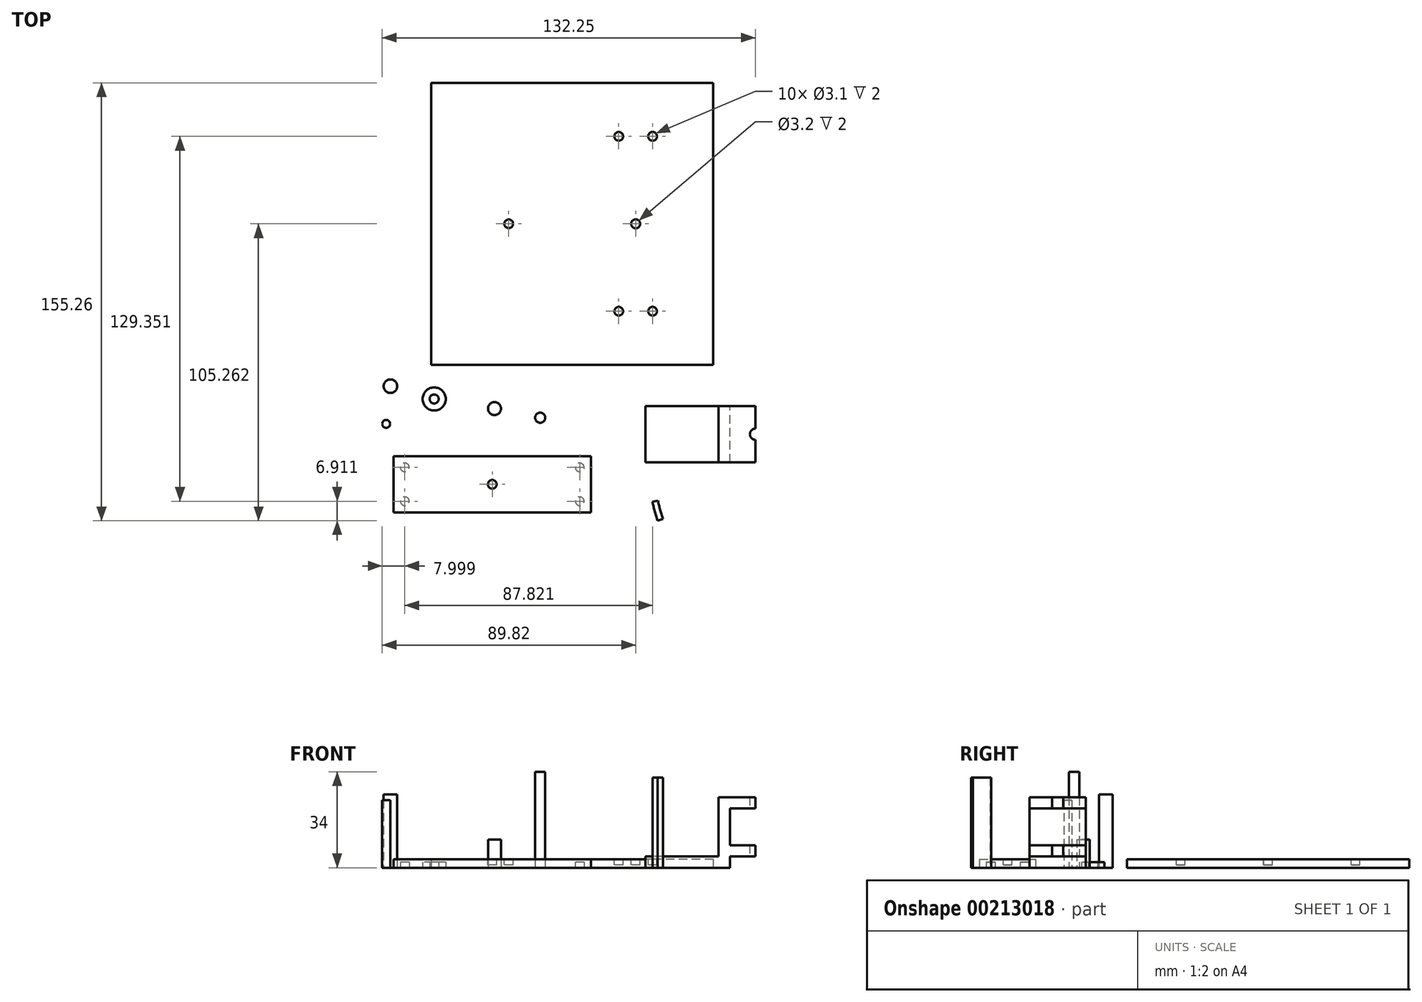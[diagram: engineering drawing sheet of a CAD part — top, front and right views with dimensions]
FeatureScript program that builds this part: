
annotation { "Feature Type Name" : "Feature", "Feature Type Description" : "" }
export const myFeature = defineFeature(function(context is Context, id is Id, definition is map)
    precondition{}
    {
        {
            var Q0;
            Q0=qCreatedBy(makeId("Top.planeOp"),FACE);
            var sketch = newSketch(context, id + "F0", { "sketchPlane" : qUnion([Q0])});
            skCircle(sketch, "E0", {"center": v(-48.92, 16) * mm, "radius": 1.6 * mm});
            skCircle(sketch, "E1", {"center": v(-48.92, 16) * mm, "radius": 4.1 * mm});
            skText(sketch, "E2", { "text": "Washer A", "fontName": "OpenSans-Regular.ttf"});
            skLineSegment(sketch, "E3.bottom", {"start": v(50, 128.1) * mm, "end": v(-50, 128.1) * mm});
            skLineSegment(sketch, "E3.top", {"start": v(50, 28.1) * mm, "end": v(-50, 28.1) * mm});
            skLineSegment(sketch, "E3.left", {"start": v(50, 128.1) * mm, "end": v(50, 28.1) * mm});
            skLineSegment(sketch, "E3.right", {"start": v(-50, 128.1) * mm, "end": v(-50, 28.1) * mm});
            skPoint(sketch, "E3.middle", {"position": v(0, 78.1) * mm});
            skLineSegment(sketch, "E4", {"start": v(-50, 78.1) * mm, "end": v(50, 78.1) * mm, "construction": true});
            skCircle(sketch, "E5", {"center": v(-64.43, 20.53) * mm, "radius": 2.4 * mm});
            skCircle(sketch, "E6", {"center": v(-28.32, -14.26) * mm, "radius": 1.6 * mm, "construction": true});
            skLineSegment(sketch, "E7.bottom", {"start": v(6.68, -24.26) * mm, "end": v(6.68, -4.26) * mm});
            skLineSegment(sketch, "E7.top", {"start": v(-63.32, -24.26) * mm, "end": v(-63.32, -4.26) * mm});
            skLineSegment(sketch, "E7.left", {"start": v(6.68, -24.26) * mm, "end": v(-63.32, -24.26) * mm});
            skLineSegment(sketch, "E7.right", {"start": v(6.68, -4.26) * mm, "end": v(-63.32, -4.26) * mm});
            skCircle(sketch, "E8", {"center": v(-59.32, -8.26) * mm, "radius": 1.55 * mm});
            skCircle(sketch, "E9", {"center": v(-59.32, -20.26) * mm, "radius": 1.55 * mm});
            skCircle(sketch, "E10", {"center": v(2.68, -8.26) * mm, "radius": 1.55 * mm});
            skCircle(sketch, "E11", {"center": v(2.68, -20.26) * mm, "radius": 1.55 * mm});
            skCircle(sketch, "E12", {"center": v(-27.53, 12.59) * mm, "radius": 2.3 * mm});
            skCircle(sketch, "E13", {"center": v(-65.92, 7.17) * mm, "radius": 1.4 * mm});
            skCircle(sketch, "E14", {"center": v(-11.34, 9.35) * mm, "radius": 1.8 * mm});
            skLineSegment(sketch, "E15.bottom", {"start": v(55.93, -6.5) * mm, "end": v(25.93, -6.5) * mm});
            skLineSegment(sketch, "E15.top", {"start": v(55.93, 13.5) * mm, "end": v(25.93, 13.5) * mm});
            skLineSegment(sketch, "E15.left", {"start": v(55.93, -6.5) * mm, "end": v(55.93, 13.5) * mm});
            skLineSegment(sketch, "E15.right", {"start": v(25.93, -6.5) * mm, "end": v(25.93, 13.5) * mm});
            skPoint(sketch, "E15.middle", {"position": v(40.93, 3.5) * mm});
            skArc(sketch, "E16", {"start": v(30.42, -20.02) * mm, "mid": v(31.18, -23.3) * mm, "end": v(32.16, -26.52) * mm});
            skLineSegment(sketch, "E17", {"start": v(32.16, -26.52) * mm, "end": v(30.27, -27.17) * mm});
            skLineSegment(sketch, "E18", {"start": v(30.42, -20.02) * mm, "end": v(28.46, -20.41) * mm});
            skArc(sketch, "E19", {"start": v(28.46, -20.41) * mm, "mid": v(29.25, -23.82) * mm, "end": v(30.27, -27.17) * mm});
            const initialGuessF0  = {"E2": [-0.05793, 0.00842, 1, 0, 0.00273]};
            skSetInitialGuess(sketch, initialGuessF0);
            skSolve(sketch);
        }
        {
            var Q0;
            Q0=makeQuery(id+"F0.imprint","IMPRINT",FACE,{"disambiguationData":[TD([[makeQuery(id+"F0.imprint","IMPRINT",EDGE,{"derivedFrom":sQuery(id+"F0.wireOp",EDGE,"E3.bottom")}),1.0]])]});
            extrude(context, id + "F1", {"entities" : qUnion([Q0]), "depth" : 3 * mm});
        }
        {
            var Q0;
            Q0=makeQuery(id+"F1.opExtrude","CAP_FACE",FACE,{"disambiguationData":[OSD([sQuery(id+"F0.wireOp",EDGE,"E3.bottom"),sQuery(id+"F0.wireOp",EDGE,"E3.top"),sQuery(id+"F0.wireOp",EDGE,"E3.left"),sQuery(id+"F0.wireOp",EDGE,"E3.right")])],"isStart":false});
            var sketch = newSketch(context, id + "F2", { "sketchPlane" : qUnion([Q0])});
            skLineSegment(sketch, "E20", {"start": v(-50, 78.1) * mm, "end": v(50, 78.1) * mm, "construction": true});
            skCircle(sketch, "E21", {"center": v(-22.5, 78.1) * mm, "radius": 1.55 * mm});
            skCircle(sketch, "E22", {"center": v(22.5, 78.1) * mm, "radius": 1.6 * mm});
            skCircle(sketch, "E23", {"center": v(-22.5, 78.1) * mm, "radius": 46 * mm, "construction": true});
            skLineSegment(sketch, "E24.bottom", {"start": v(32.5, 113.1) * mm, "end": v(12.5, 113.1) * mm, "construction": true});
            skLineSegment(sketch, "E24.top", {"start": v(32.5, 43.1) * mm, "end": v(12.5, 43.1) * mm, "construction": true});
            skLineSegment(sketch, "E24.left", {"start": v(32.5, 113.1) * mm, "end": v(32.5, 43.1) * mm, "construction": true});
            skLineSegment(sketch, "E24.right", {"start": v(12.5, 113.1) * mm, "end": v(12.5, 43.1) * mm, "construction": true});
            skCircle(sketch, "E25", {"center": v(16.5, 47.1) * mm, "radius": 1.55 * mm});
            skCircle(sketch, "E26", {"center": v(28.5, 47.1) * mm, "radius": 1.55 * mm});
            skCircle(sketch, "E27", {"center": v(16.5, 109.1) * mm, "radius": 1.55 * mm});
            skCircle(sketch, "E28", {"center": v(28.5, 109.1) * mm, "radius": 1.55 * mm});
            skSolve(sketch);
        }
        {
            var Q0;
            Q0=makeQuery(id+"F2.imprint","IMPRINT",FACE,{"disambiguationData":[TD([[makeQuery(id+"F2.imprint","IMPRINT",EDGE,{"derivedFrom":sQuery(id+"F2.wireOp",EDGE,"E21")}),1.0]])]});
            var Q1;
            Q1=makeQuery(id+"F2.imprint","IMPRINT",FACE,{"disambiguationData":[TD([[makeQuery(id+"F2.imprint","IMPRINT",EDGE,{"derivedFrom":sQuery(id+"F2.wireOp",EDGE,"E22")}),1.0]])]});
            extrude(context, id + "F3", {"entities" : qUnion([Q0, Q1]), "operationType" : NewBodyOperationType.REMOVE, "oppositeDirection" : true, "depth" : 2 * mm});
        }
        {
            var Q0;
            Q0=makeQuery(id+"F0.imprint","IMPRINT",FACE,{"disambiguationData":[TD([[makeQuery(id+"F0.imprint","IMPRINT",EDGE,{"derivedFrom":sQuery(id+"F0.wireOp",EDGE,"E5")}),1.0]])]});
            extrude(context, id + "F4", {"entities" : qUnion([Q0]), "depth" : 26 * mm});
        }
        {
            var Q0;
            Q0=makeQuery(id+"F0.imprint","IMPRINT",FACE,{"disambiguationData":[TD([[makeQuery(id+"F0.imprint","IMPRINT",EDGE,{"derivedFrom":sQuery(id+"F0.wireOp",EDGE,"E0")}),-1.0]])]});
            extrude(context, id + "F5", {"entities" : qUnion([Q0]), "depth" : 2 * mm});
        }
        {
            var Q0;
            Q0=makeQuery(id+"F0.imprint","IMPRINT",FACE,{"disambiguationData":[TD([[makeQuery(id+"F0.imprint","IMPRINT",EDGE,{"derivedFrom":sQuery(id+"F0.wireOp",EDGE,"E7.bottom")}),1.0]])]});
            var Q1;
            Q1=makeQuery(id+"F0.imprint","IMPRINT",FACE,{"disambiguationData":[TD([[makeQuery(id+"F0.imprint","IMPRINT",EDGE,{"derivedFrom":sQuery(id+"F0.wireOp",EDGE,"E8")}),1.0]])]});
            var Q2;
            Q2=makeQuery(id+"F0.imprint","IMPRINT",FACE,{"disambiguationData":[TD([[makeQuery(id+"F0.imprint","IMPRINT",EDGE,{"derivedFrom":sQuery(id+"F0.wireOp",EDGE,"E9")}),1.0]])]});
            var Q3;
            Q3=makeQuery(id+"F0.imprint","IMPRINT",FACE,{"disambiguationData":[TD([[makeQuery(id+"F0.imprint","IMPRINT",EDGE,{"derivedFrom":sQuery(id+"F0.wireOp",EDGE,"E10")}),1.0]])]});
            var Q4;
            Q4=makeQuery(id+"F0.imprint","IMPRINT",FACE,{"disambiguationData":[TD([[makeQuery(id+"F0.imprint","IMPRINT",EDGE,{"derivedFrom":sQuery(id+"F0.wireOp",EDGE,"E11")}),1.0]])]});
            extrude(context, id + "F6", {"entities" : qUnion([Q0, Q1, Q2, Q3, Q4]), "depth" : 3 * mm});
        }
        {
            var Q0;
            Q0=makeQuery(id+"F0.imprint","IMPRINT",FACE,{"disambiguationData":[TD([[makeQuery(id+"F0.imprint","IMPRINT",EDGE,{"derivedFrom":sQuery(id+"F0.wireOp",EDGE,"E10")}),1.0]])]});
            var Q1;
            Q1=makeQuery(id+"F0.imprint","IMPRINT",FACE,{"disambiguationData":[TD([[makeQuery(id+"F0.imprint","IMPRINT",EDGE,{"derivedFrom":sQuery(id+"F0.wireOp",EDGE,"E11")}),1.0]])]});
            var Q2;
            Q2=makeQuery(id+"F0.imprint","IMPRINT",FACE,{"disambiguationData":[TD([[makeQuery(id+"F0.imprint","IMPRINT",EDGE,{"derivedFrom":sQuery(id+"F0.wireOp",EDGE,"E8")}),1.0]])]});
            var Q3;
            Q3=makeQuery(id+"F0.imprint","IMPRINT",FACE,{"disambiguationData":[TD([[makeQuery(id+"F0.imprint","IMPRINT",EDGE,{"derivedFrom":sQuery(id+"F0.wireOp",EDGE,"E9")}),1.0]])]});
            extrude(context, id + "F7", {"entities" : qUnion([Q0, Q1, Q2, Q3]), "operationType" : NewBodyOperationType.REMOVE, "depth" : 2 * mm});
        }
        {
            var Q0;
            Q0=makeQuery(id+"F6.opExtrude","CAP_FACE",FACE,{"disambiguationData":[OSD([sQuery(id+"F0.wireOp",EDGE,"E7.bottom"),sQuery(id+"F0.wireOp",EDGE,"E7.top"),sQuery(id+"F0.wireOp",EDGE,"E7.left"),sQuery(id+"F0.wireOp",EDGE,"E7.right")])],"isStart":false});
            var sketch = newSketch(context, id + "F8", { "sketchPlane" : qUnion([Q0])});
            skCircle(sketch, "E29", {"center": v(-28.32, -14.26) * mm, "radius": 1.55 * mm});
            skSolve(sketch);
        }
        {
            var Q0;
            Q0=makeQuery(id+"F8.imprint","IMPRINT",FACE,{"disambiguationData":[TD([[makeQuery(id+"F8.imprint","IMPRINT",EDGE,{"derivedFrom":sQuery(id+"F8.wireOp",EDGE,"E29")}),1.0]])]});
            extrude(context, id + "F9", {"entities" : qUnion([Q0]), "operationType" : NewBodyOperationType.REMOVE, "oppositeDirection" : true, "depth" : 2 * mm});
        }
        {
            var Q0;
            Q0=makeQuery(id+"F2.imprint","IMPRINT",FACE,{"disambiguationData":[TD([[makeQuery(id+"F2.imprint","IMPRINT",EDGE,{"derivedFrom":sQuery(id+"F2.wireOp",EDGE,"E28")}),1.0]])]});
            var Q1;
            Q1=makeQuery(id+"F2.imprint","IMPRINT",FACE,{"disambiguationData":[TD([[makeQuery(id+"F2.imprint","IMPRINT",EDGE,{"derivedFrom":sQuery(id+"F2.wireOp",EDGE,"E27")}),1.0]])]});
            var Q2;
            Q2=makeQuery(id+"F2.imprint","IMPRINT",FACE,{"disambiguationData":[TD([[makeQuery(id+"F2.imprint","IMPRINT",EDGE,{"derivedFrom":sQuery(id+"F2.wireOp",EDGE,"E25")}),1.0]])]});
            var Q3;
            Q3=makeQuery(id+"F2.imprint","IMPRINT",FACE,{"disambiguationData":[TD([[makeQuery(id+"F2.imprint","IMPRINT",EDGE,{"derivedFrom":sQuery(id+"F2.wireOp",EDGE,"E26")}),1.0]])]});
            extrude(context, id + "F10", {"entities" : qUnion([Q0, Q1, Q2, Q3]), "operationType" : NewBodyOperationType.REMOVE, "oppositeDirection" : true, "depth" : 2 * mm});
        }
        {
            var Q0;
            Q0=makeQuery(id+"F0.imprint","IMPRINT",FACE,{"disambiguationData":[TD([[makeQuery(id+"F0.imprint","IMPRINT",EDGE,{"derivedFrom":sQuery(id+"F0.wireOp",EDGE,"E12")}),1.0]])]});
            extrude(context, id + "F11", {"entities" : qUnion([Q0]), "depth" : 10 * mm});
        }
        {
            var Q0;
            Q0=makeQuery(id+"F0.imprint","IMPRINT",FACE,{"disambiguationData":[TD([[makeQuery(id+"F0.imprint","IMPRINT",EDGE,{"derivedFrom":sQuery(id+"F0.wireOp",EDGE,"E13")}),1.0]])]});
            extrude(context, id + "F12", {"entities" : qUnion([Q0]), "depth" : 24 * mm});
        }
        {
            var Q0;
            Q0=makeQuery(id+"F0.imprint","IMPRINT",FACE,{"disambiguationData":[TD([[makeQuery(id+"F0.imprint","IMPRINT",EDGE,{"derivedFrom":sQuery(id+"F0.wireOp",EDGE,"E14")}),1.0]])]});
            extrude(context, id + "F13", {"entities" : qUnion([Q0]), "depth" : 34 * mm});
        }
        {
            var Q0;
            Q0=makeQuery(id+"F0.imprint","IMPRINT",FACE,{"disambiguationData":[TD([[makeQuery(id+"F0.imprint","IMPRINT",EDGE,{"derivedFrom":sQuery(id+"F0.wireOp",EDGE,"E15.bottom")}),-1.0]])]});
            extrude(context, id + "F14", {"entities" : qUnion([Q0]), "depth" : 4 * mm});
        }
        {
            var Q0;
            Q0=makeQuery(id+"F14.opExtrude","CAP_FACE",FACE,{"disambiguationData":[OSD([sQuery(id+"F0.wireOp",EDGE,"E15.bottom"),sQuery(id+"F0.wireOp",EDGE,"E15.top"),sQuery(id+"F0.wireOp",EDGE,"E15.left"),sQuery(id+"F0.wireOp",EDGE,"E15.right")])],"isStart":false});
            var sketch = newSketch(context, id + "F15", { "sketchPlane" : qUnion([Q0])});
            skLineSegment(sketch, "E30.bottom", {"start": v(55.93, 13.5) * mm, "end": v(51.93, 13.5) * mm});
            skLineSegment(sketch, "E30.top", {"start": v(55.93, -6.5) * mm, "end": v(51.93, -6.5) * mm});
            skLineSegment(sketch, "E30.left", {"start": v(55.93, 13.5) * mm, "end": v(55.93, -6.5) * mm});
            skLineSegment(sketch, "E30.right", {"start": v(51.93, 13.5) * mm, "end": v(51.93, -6.5) * mm});
            skLineSegment(sketch, "E31.bottom", {"start": v(55.93, 13.5) * mm, "end": v(64.93, 13.5) * mm});
            skLineSegment(sketch, "E31.top", {"start": v(55.93, -6.5) * mm, "end": v(64.93, -6.5) * mm});
            skLineSegment(sketch, "E31.right", {"start": v(64.93, 13.5) * mm, "end": v(64.93, -6.5) * mm});
            skCircle(sketch, "E32", {"center": v(64.93, 3.5) * mm, "radius": 1.95 * mm});
            skSolve(sketch);
        }
        {
            var Q0;
            Q0=makeQuery(id+"F15.imprint","IMPRINT",FACE,{"disambiguationData":[TD([[makeQuery(id+"F15.imprint","IMPRINT",EDGE,{"derivedFrom":sQuery(id+"F15.wireOp",EDGE,"E30.bottom")}),1.0]])]});
            extrude(context, id + "F16", {"entities" : qUnion([Q0]), "operationType" : NewBodyOperationType.ADD, "depth" : 21 * mm});
        }
        {
            var Q0;
            Q0=makeQuery(id+"F16.opExtrude","CAP_FACE",FACE,{"disambiguationData":[OSD([sQuery(id+"F15.wireOp",EDGE,"E30.bottom"),sQuery(id+"F15.wireOp",EDGE,"E30.top"),sQuery(id+"F15.wireOp",EDGE,"E30.left"),sQuery(id+"F15.wireOp",EDGE,"E30.right")])],"isStart":false});
            var sketch = newSketch(context, id + "F17", { "sketchPlane" : qUnion([Q0])});
            skLineSegment(sketch, "E33.bottom", {"start": v(51.93, 13.5) * mm, "end": v(64.93, 13.5) * mm});
            skLineSegment(sketch, "E33.top", {"start": v(51.93, -6.5) * mm, "end": v(64.93, -6.5) * mm});
            skLineSegment(sketch, "E33.left", {"start": v(51.93, 13.5) * mm, "end": v(51.93, -6.5) * mm});
            skLineSegment(sketch, "E33.right", {"start": v(64.93, 13.5) * mm, "end": v(64.93, -6.5) * mm});
            skSolve(sketch);
        }
        {
            var Q0;
            Q0 = qSketchRegion(id + "F17", true);
            extrude(context, id + "F18", {"entities" : qUnion([Q0]), "operationType" : NewBodyOperationType.ADD, "oppositeDirection" : true, "depth" : 4 * mm});
        }
        {
            var Q0;
            Q0=makeQuery(id+"F15.imprint","IMPRINT",FACE,{"disambiguationData":[TD([[makeQuery(id+"F15.imprint","IMPRINT",EDGE,{"derivedFrom":sQuery(id+"F15.wireOp",EDGE,"E31.bottom")}),-1.0]])]});
            var Q1;
            {var subQ0=sQuery(id+"F15.wireOp",EDGE,"E32");var subQ1=sQuery(id+"F15.wireOp",EDGE,"E31.right");var subQ2=makeQuery(id+"F15.imprint","INTERSECT",VERTEX,{"disambiguationData":[OD(0.0)],"derivedFrom":[subQ1,subQ0]});Q1=makeQuery(id+"F15.imprint","IMPRINT",FACE,{"disambiguationData":[TD([[makeQuery(id+"F15.imprint","IMPRINT",EDGE,{"disambiguationData":[TD([[subQ2,-1.0]])],"derivedFrom":subQ1}),-1.0]])]});}
            extrude(context, id + "F19", {"entities" : qUnion([Q0, Q1]), "operationType" : NewBodyOperationType.ADD, "depth" : 4 * mm});
        }
        {
            var Q0;
            {var subQ0=sQuery(id+"F15.wireOp",EDGE,"E32");var subQ1=sQuery(id+"F15.wireOp",EDGE,"E31.right");var subQ2=makeQuery(id+"F15.imprint","INTERSECT",VERTEX,{"disambiguationData":[OD(0.0)],"derivedFrom":[subQ1,subQ0]});Q0=makeQuery(id+"F15.imprint","IMPRINT",FACE,{"disambiguationData":[TD([[makeQuery(id+"F15.imprint","IMPRINT",EDGE,{"disambiguationData":[TD([[subQ2,-1.0]])],"derivedFrom":subQ1}),-1.0]])]});}
            var Q1;
            {var subQ0=sQuery(id+"F15.wireOp",EDGE,"E32");var subQ1=sQuery(id+"F15.wireOp",EDGE,"E31.right");var subQ2=makeQuery(id+"F15.imprint","INTERSECT",VERTEX,{"disambiguationData":[OD(0.0)],"derivedFrom":[subQ1,subQ0]});Q1=makeQuery(id+"F15.imprint","IMPRINT",FACE,{"disambiguationData":[TD([[makeQuery(id+"F15.imprint","IMPRINT",EDGE,{"disambiguationData":[TD([[subQ2,-1.0]])],"derivedFrom":subQ1}),1.0]])]});}
            extrude(context, id + "F20", {"entities" : qUnion([Q0, Q1]), "operationType" : NewBodyOperationType.REMOVE, "endBound" : BoundingType.THROUGH_ALL, "depth" : 25 * mm});
        }
        {
            var Q0;
            Q0=makeQuery(id+"F0.imprint","IMPRINT",FACE,{"disambiguationData":[TD([[makeQuery(id+"F0.imprint","IMPRINT",EDGE,{"derivedFrom":sQuery(id+"F0.wireOp",EDGE,"E16")}),-1.0]])]});
            extrude(context, id + "F21", {"entities" : qUnion([Q0]), "depth" : 32 * mm});
        }
    });
